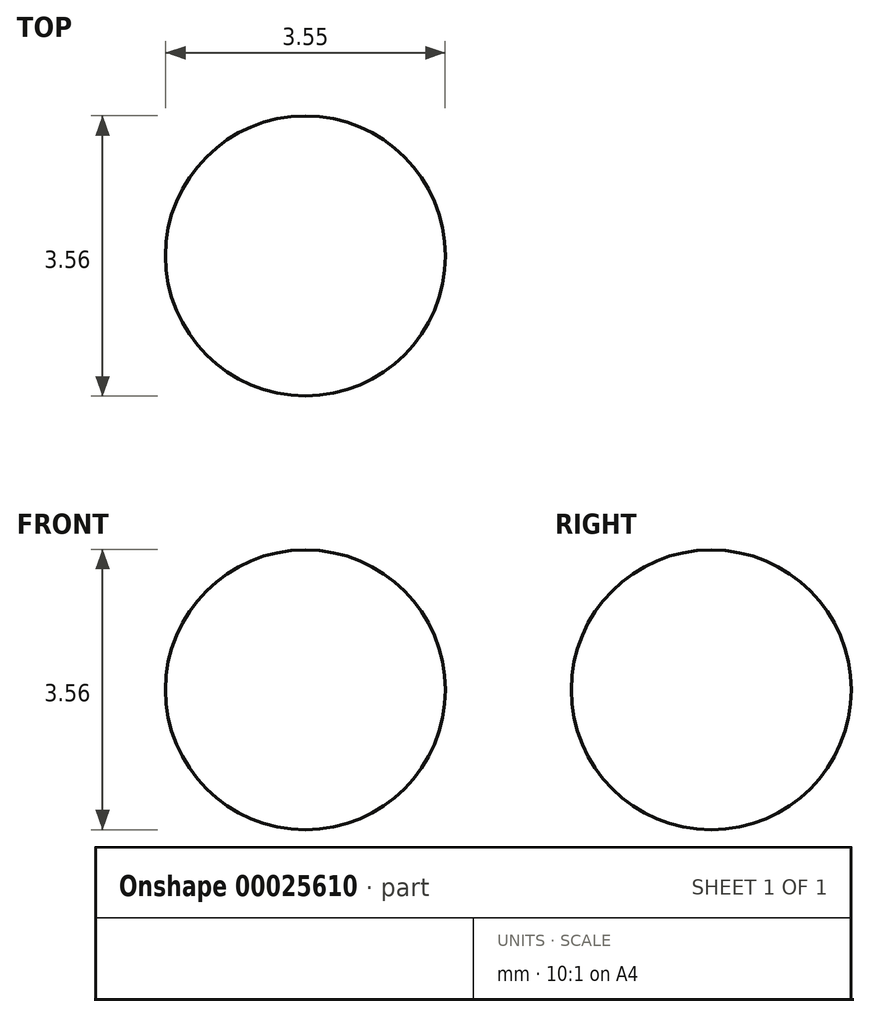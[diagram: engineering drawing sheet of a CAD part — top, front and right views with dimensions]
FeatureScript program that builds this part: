
annotation { "Feature Type Name" : "Feature", "Feature Type Description" : "" }
export const myFeature = defineFeature(function(context is Context, id is Id, definition is map)
    precondition{}
    {
        {
            var Q0;
            Q0=qCreatedBy(makeId("Front.planeOp"),FACE);
            var sketch = newSketch(context, id + "F0", { "sketchPlane" : qUnion([Q0])});
            skArc(sketch, "E0", {"start": v(-11.27, 15.06) * mm, "mid": v(-13.05, 13.28) * mm, "end": v(-11.27, 11.5) * mm});
            skLineSegment(sketch, "E1", {"start": v(-11.27, 15.06) * mm, "end": v(-11.27, 11.5) * mm});
            skSolve(sketch);
        }
        {
            var Q0;
            Q0=makeQuery(id+"F0.imprint","IMPRINT",FACE,{"disambiguationData":[TD([[makeQuery(id+"F0.imprint","IMPRINT",EDGE,{"derivedFrom":sQuery(id+"F0.wireOp",EDGE,"E0")}),1.0]])]});
            var Q1;
            Q1=sQuery(id+"F0.wireOp",EDGE,"E1");
            revolve(context, id + "F1", {"entities" : qUnion([Q0]), "axis" : qUnion([Q1]), "revolveType" : RevolveType.FULL});
        }
    });
